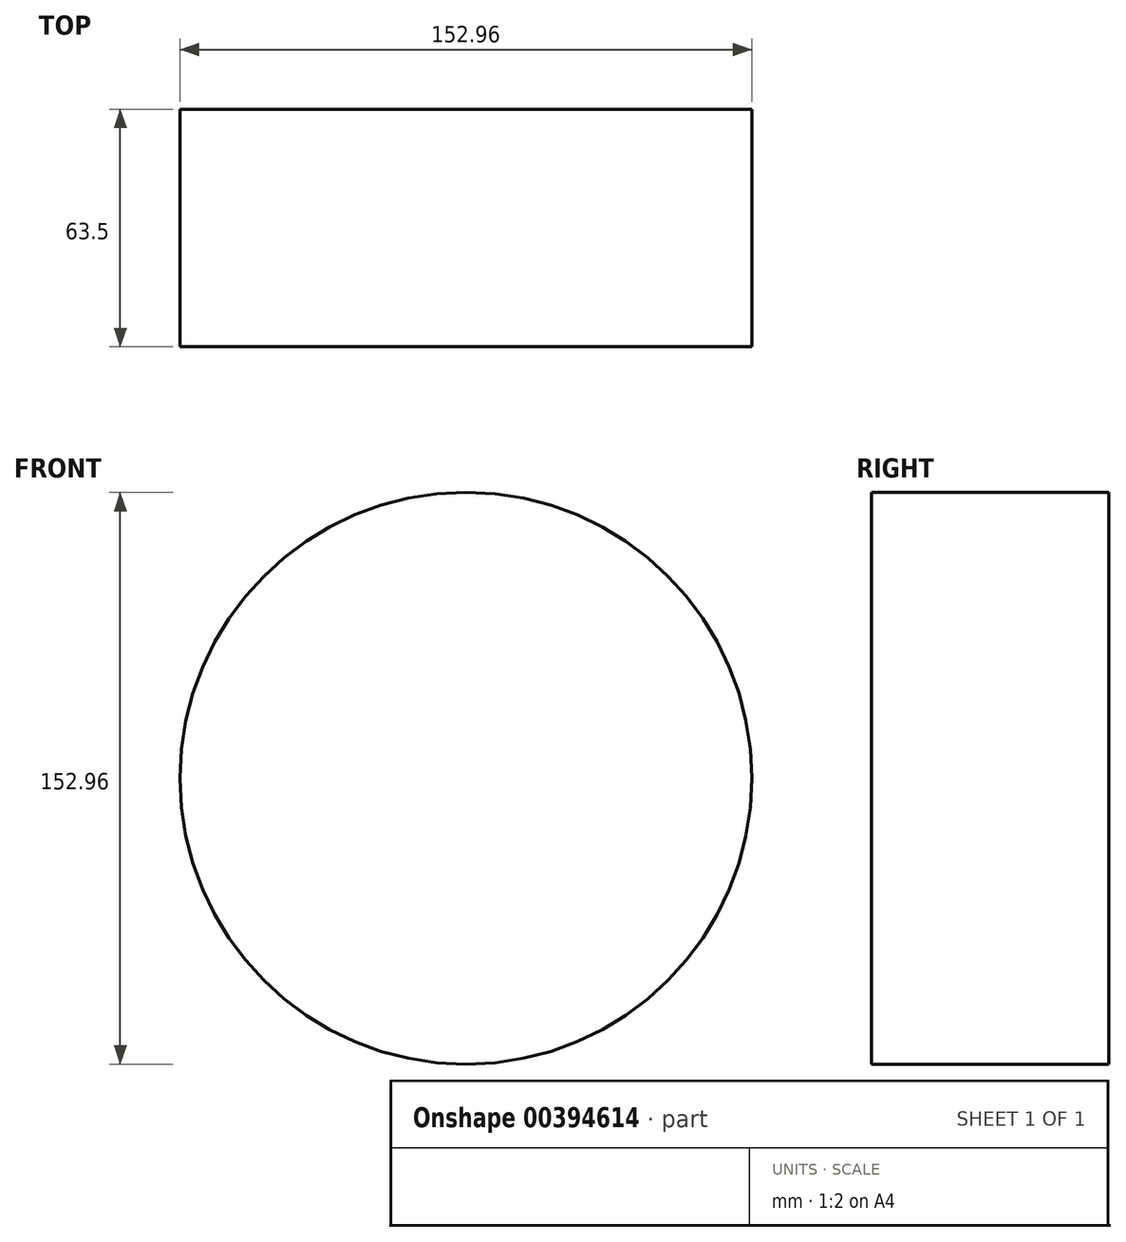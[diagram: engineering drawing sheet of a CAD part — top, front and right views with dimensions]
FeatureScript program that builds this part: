
annotation { "Feature Type Name" : "Feature", "Feature Type Description" : "" }
export const myFeature = defineFeature(function(context is Context, id is Id, definition is map)
    precondition{}
    {
        {
            var Q0;
            Q0=qCreatedBy(makeId("Front.planeOp"),FACE);
            var sketch = newSketch(context, id + "F0", { "sketchPlane" : qUnion([Q0])});
            skCircle(sketch, "E0", {"center": v(0, 0) * mm, "radius": 76.48 * mm});
            skSolve(sketch);
        }
        {
            var Q0;
            Q0=makeQuery(id+"F0.imprint","IMPRINT",FACE,{"disambiguationData":[TD([[makeQuery(id+"F0.imprint","IMPRINT",EDGE,{"derivedFrom":sQuery(id+"F0.wireOp",EDGE,"E0")}),1.0]])]});
            extrude(context, id + "F1", {"entities" : qUnion([Q0]), "depth" : 63.5 * mm});
        }
    });
